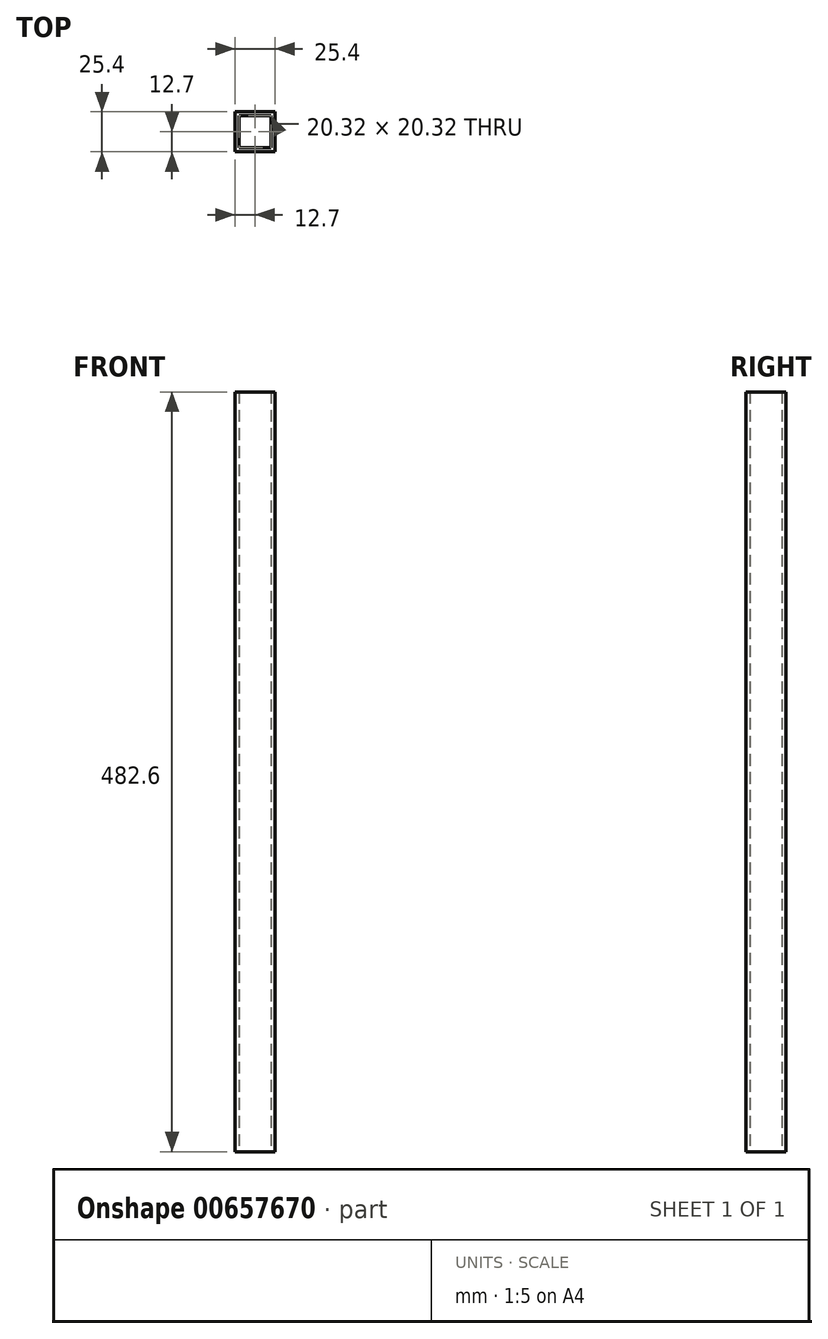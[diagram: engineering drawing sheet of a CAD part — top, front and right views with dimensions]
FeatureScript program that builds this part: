
annotation { "Feature Type Name" : "Feature", "Feature Type Description" : "" }
export const myFeature = defineFeature(function(context is Context, id is Id, definition is map)
    precondition{}
    {
        {
            var Q0;
            Q0=qCreatedBy(makeId("Top.planeOp"),FACE);
            var sketch = newSketch(context, id + "F0", { "sketchPlane" : qUnion([Q0])});
            skLineSegment(sketch, "E0.bottom", {"start": v(0, 0) * mm, "end": v(25.4, 0) * mm});
            skLineSegment(sketch, "E0.top", {"start": v(0, -25.4) * mm, "end": v(25.4, -25.4) * mm});
            skLineSegment(sketch, "E0.left", {"start": v(0, 0) * mm, "end": v(0, -25.4) * mm});
            skLineSegment(sketch, "E0.right", {"start": v(25.4, 0) * mm, "end": v(25.4, -25.4) * mm});
            skLineSegment(sketch, "E1.bottom", {"start": v(2.54, -2.54) * mm, "end": v(22.86, -2.54) * mm});
            skLineSegment(sketch, "E1.top", {"start": v(2.54, -22.86) * mm, "end": v(22.86, -22.86) * mm});
            skLineSegment(sketch, "E1.left", {"start": v(2.54, -2.54) * mm, "end": v(2.54, -22.86) * mm});
            skLineSegment(sketch, "E1.right", {"start": v(22.86, -2.54) * mm, "end": v(22.86, -22.86) * mm});
            skSolve(sketch);
        }
        {
            var Q0;
            Q0=makeQuery(id+"F0.imprint","IMPRINT",FACE,{"disambiguationData":[TD([[makeQuery(id+"F0.imprint","IMPRINT",EDGE,{"derivedFrom":sQuery(id+"F0.wireOp",EDGE,"E0.bottom")}),-1.0]])]});
            extrude(context, id + "F1", {"entities" : qUnion([Q0]), "depth" : 482.6 * mm, "offsetDistance" : 25.4 * mm});
        }
    });
